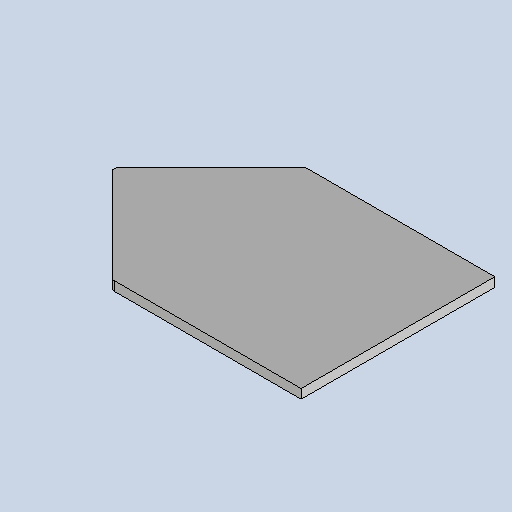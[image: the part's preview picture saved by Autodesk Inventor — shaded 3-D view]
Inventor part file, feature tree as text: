
AUTODESK INVENTOR PART (.ipt)
format: ipt  version: 2025 (Build 290162010, 162A)  size: 237,568 bytes
history: native  units: mm
features: sheet_metal_op x1, chamfer x1, sketch x1, other x1
ambient origin geometry x8: Origin, YZ Plane, XZ Plane, XY Plane, X Axis, Y Axis, Z Axis, Center Point
bodies: Solid1 (feature_tree)
feature tree (4):
  sheet_metal_op  "Face1"
  chamfer  "Corner Round2"
  sketch  "Sketch1"  dims[d0=41.0mm d1=42.0mm d2=2.0mm d4=62.0mm d6=1.0mm]
  other  "Plate1"
